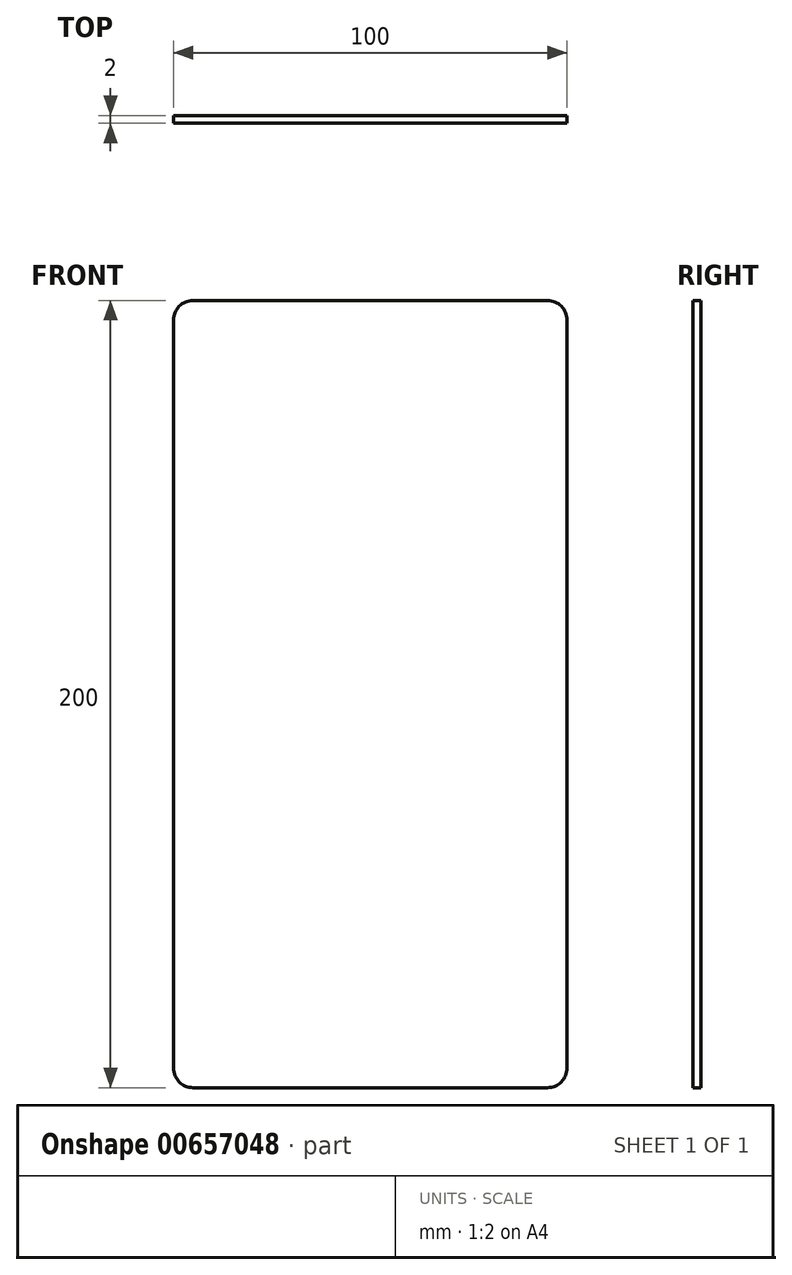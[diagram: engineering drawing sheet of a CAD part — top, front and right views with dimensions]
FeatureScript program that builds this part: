
annotation { "Feature Type Name" : "Feature", "Feature Type Description" : "" }
export const myFeature = defineFeature(function(context is Context, id is Id, definition is map)
    precondition{}
    {
        {
            var Q0;
            Q0=qCreatedBy(makeId("Front.planeOp"),FACE);
            var sketch = newSketch(context, id + "F0", { "sketchPlane" : qUnion([Q0])});
            skLineSegment(sketch, "E0.bottom", {"start": v(-5, 0) * mm, "end": v(-95, 0) * mm});
            skLineSegment(sketch, "E0.top", {"start": v(-5, 200) * mm, "end": v(-95, 200) * mm});
            skLineSegment(sketch, "E0.left", {"start": v(0, 5) * mm, "end": v(0, 195) * mm});
            skLineSegment(sketch, "E0.right", {"start": v(-100, 5) * mm, "end": v(-100, 195) * mm});
            skPoint(sketch, "E1.visualSharp", {"position": v(-100, 200) * mm});
            skArc(sketch, "E1.filletArc", {"start": v(-95, 200) * mm, "mid": v(-98.54, 198.54) * mm, "end": v(-100, 195) * mm});
            skPoint(sketch, "E2.visualSharp", {"position": v(0, 200) * mm});
            skArc(sketch, "E2.filletArc", {"start": v(0, 195) * mm, "mid": v(-1.46, 198.54) * mm, "end": v(-5, 200) * mm});
            skPoint(sketch, "E3.visualSharp", {"position": v(-100, 0) * mm});
            skArc(sketch, "E3.filletArc", {"start": v(-100, 5) * mm, "mid": v(-98.54, 1.46) * mm, "end": v(-95, 0) * mm});
            skPoint(sketch, "E4.visualSharp", {"position": v(0, 0) * mm});
            skArc(sketch, "E4.filletArc", {"start": v(-5, 0) * mm, "mid": v(-1.46, 1.46) * mm, "end": v(0, 5) * mm});
            skSolve(sketch);
        }
        {
            var Q0;
            Q0=makeQuery(id+"F0.imprint","IMPRINT",FACE,{"disambiguationData":[TD([[makeQuery(id+"F0.imprint","IMPRINT",EDGE,{"derivedFrom":sQuery(id+"F0.wireOp",EDGE,"E0.bottom")}),-1.0]])]});
            extrude(context, id + "F1", {"entities" : qUnion([Q0]), "depth" : 2 * mm, "offsetDistance" : 25 * mm});
        }
    });
